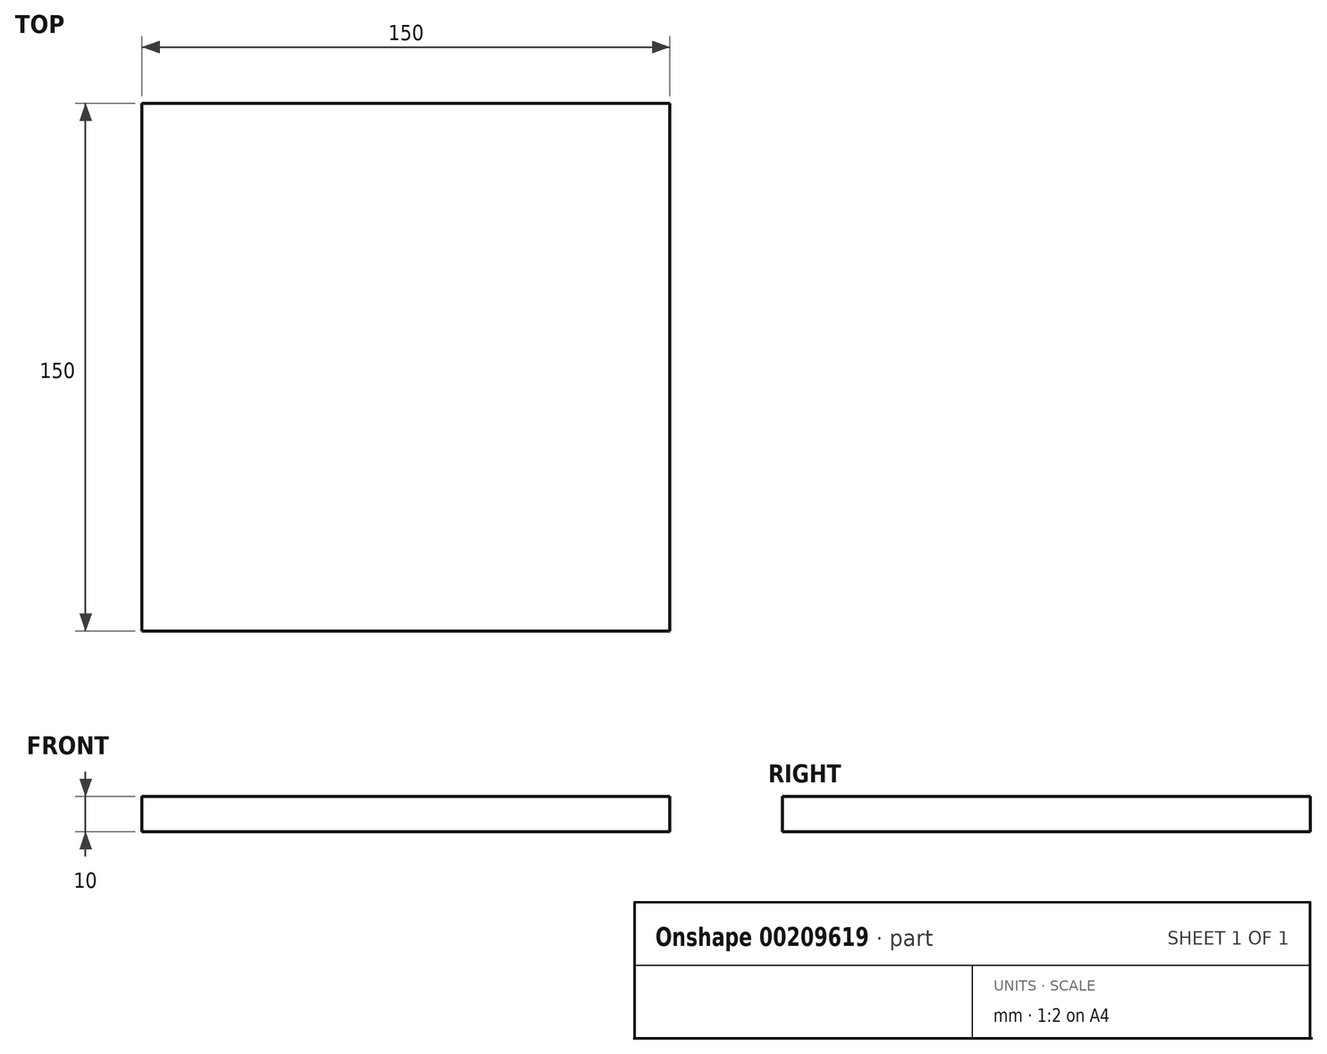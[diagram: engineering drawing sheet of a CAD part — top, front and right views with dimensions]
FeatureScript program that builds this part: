
annotation { "Feature Type Name" : "Feature", "Feature Type Description" : "" }
export const myFeature = defineFeature(function(context is Context, id is Id, definition is map)
    precondition{}
    {
        {
            var Q0;
            Q0=qCreatedBy(makeId("Top.planeOp"),FACE);
            var sketch = newSketch(context, id + "F0", { "sketchPlane" : qUnion([Q0])});
            skLineSegment(sketch, "E0.bottom", {"start": v(75, 75) * mm, "end": v(-75, 75) * mm});
            skLineSegment(sketch, "E0.top", {"start": v(75, -75) * mm, "end": v(-75, -75) * mm});
            skLineSegment(sketch, "E0.left", {"start": v(75, 75) * mm, "end": v(75, -75) * mm});
            skLineSegment(sketch, "E0.right", {"start": v(-75, 75) * mm, "end": v(-75, -75) * mm});
            skPoint(sketch, "E0.middle", {"position": v(0, 0) * mm});
            skSolve(sketch);
        }
        {
            var Q0;
            Q0 = qSketchRegion(id + "F0", true);
            extrude(context, id + "F1", {"entities" : qUnion([Q0]), "depth" : 10 * mm});
        }
    });
